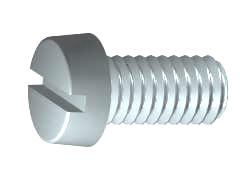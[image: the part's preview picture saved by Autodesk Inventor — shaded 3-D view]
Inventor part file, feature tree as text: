
AUTODESK INVENTOR PART (.ipt)
format: ipt  version: unknown  size: 272,896 bytes
history: native  units: mm (DEFAULTED — no unit token found)
features: other x1, extrude x1, plane x1
ambient origin geometry x7: Origin, YZ Plane, XZ Plane, X Axis, Y Axis, Z Axis, Center Point
feature tree (3):
  other  "Körper"
  extrude  "Loch"  Depth=16.0mm
  plane  "Work Plane1"
